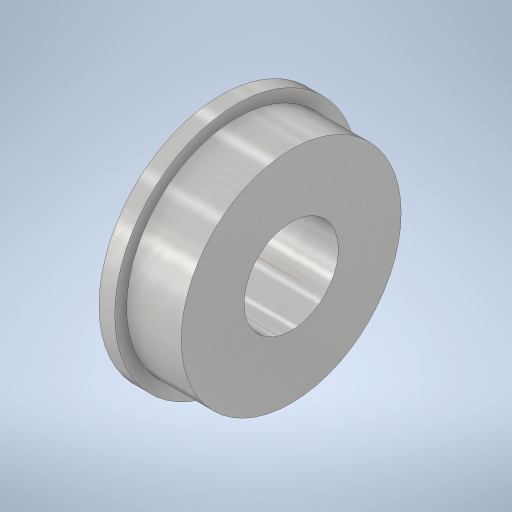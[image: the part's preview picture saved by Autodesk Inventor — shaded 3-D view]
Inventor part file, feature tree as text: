
AUTODESK INVENTOR PART (.ipt)
format: ipt  version: 2023.3 (Build 273359000, 359)  size: 289,280 bytes
history: native  units: in
note: dims shown in document units (in); Inventor stores cm internally (conversion verified against a paired STEP export)
features: revolve x1
ambient origin geometry x8: Origin, YZ Plane, XZ Plane, XY Plane, X Axis, Y Axis, Z Axis, Center Point
bodies: Solid1 (feature_tree)
feature tree (1):
  revolve  "Revolve1"  [1 undecoded]
note: 1 required parameter value undecoded (feature->parameter linkage not recoverable at this tier; creation-order binding heuristic only, values carry confidence <= 0.55)
